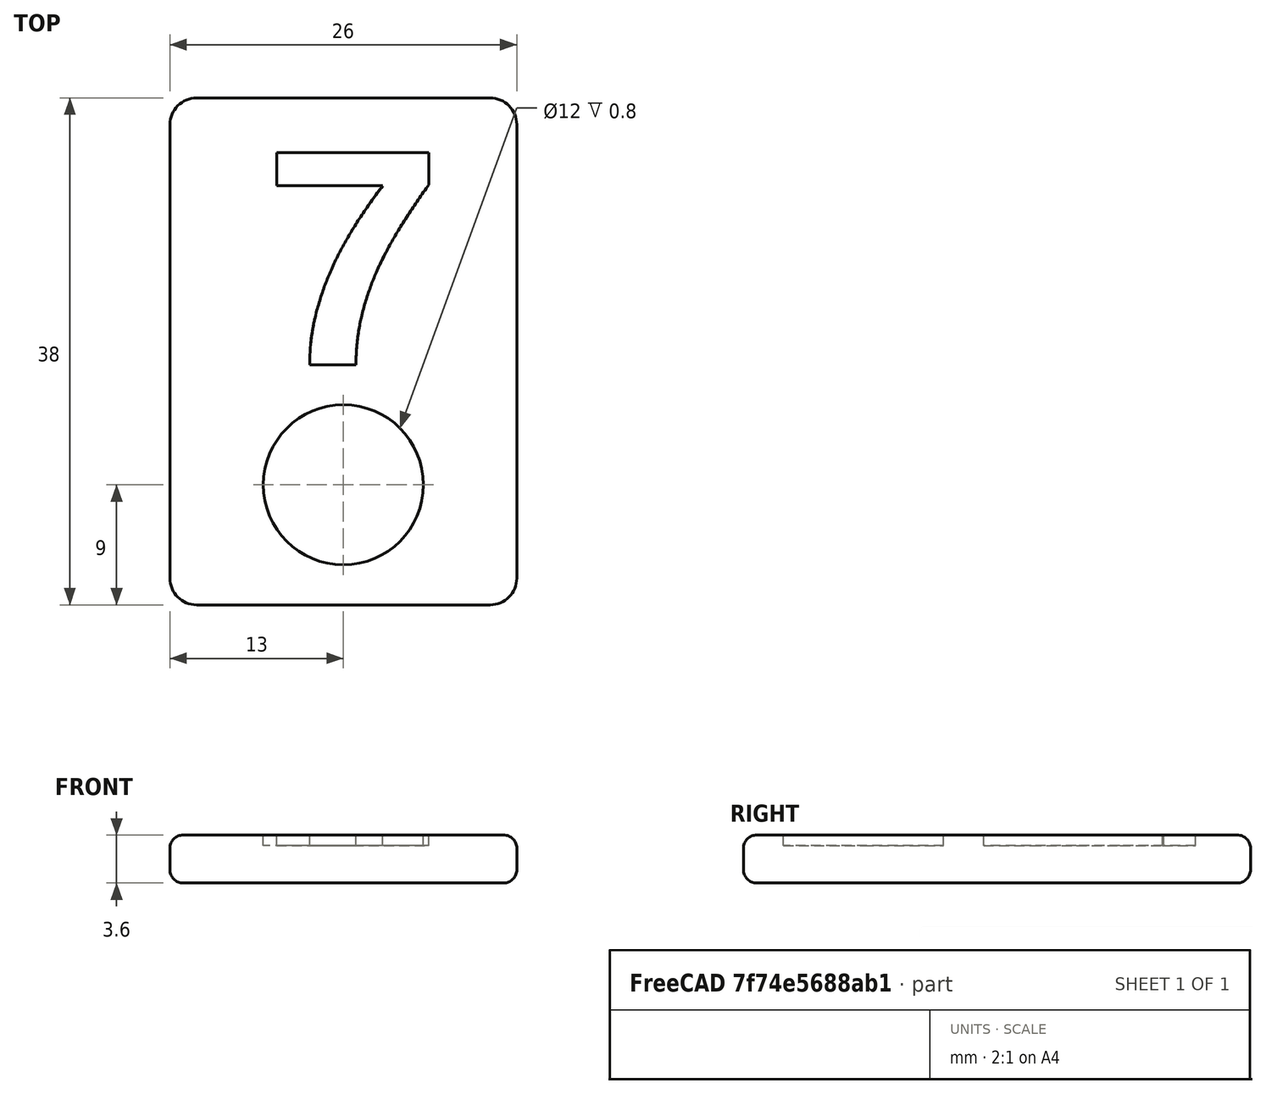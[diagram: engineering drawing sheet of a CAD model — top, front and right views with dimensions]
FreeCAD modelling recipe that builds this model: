
FCSTD DOCUMENT  (FreeCAD 0.14R3702 (Git))
Label: ficha7
License: CC-BY 3.0
LicenseURL: http://creativecommons.org/licenses/by/3.0/
objects: Part::Fillet×2, Part::Cut×2, Part::Box×1, Part::Part2DObjectPython×1, Part::Cylinder×1, Part::Extrusion×1
note: 8 computed .brp shape members not serialized (recipe doc carries the construction recipe); baked Part::Feature solids carry a one-line shape summary decoded from their .brp

FEATURE [Part::Box] Box  label="Cubo"
  Height = 3.6
  Length = 26
  Width = 38
FEATURE [Part::Fillet] Fillet
  Base = -> Box
  Edges = 4 edges r=2: [Edge1,Edge3,Edge5,Edge7]
FEATURE [Part::Part2DObjectPython] ShapeString  # Draft 2D object (typed FeaturePython)
  FontFile = <path>
  Placement = pos=(6.5,18,4) rot=(0,0,1;0rad)
  Size = 18
  String = 7
  Tracking = 0
FEATURE [Part::Cylinder] Cylinder  label="Cilindro"
  Angle = 360
  Height = 10
  Placement = pos=(13,9,2.8) rot=(0,0,1;0rad)
  Radius = 6
FEATURE [Part::Extrusion] Extrude001
  Base = -> ShapeString
  Dir = (0,0,2)
  Placement = pos=(0,0,-1.2) rot=(0,0,1;0rad)
  Solid = true
FEATURE [Part::Cut] Cut
  Base = -> Fillet
  Tool = -> Cylinder
FEATURE [Part::Cut] Cut001
  Base = -> Cut
  Tool = -> Extrude001
FEATURE [Part::Fillet] Fillet001
  Base = -> Cut001
  Edges = 16 edges r=1: [Edge1,Edge4,Edge20,Edge21,Edge22,Edge23,Edge24,Edge25,Edge26,Edge27,Edge29,Edge31,Edge32,Edge33,Edge34,Edge35]
note: 1 file-system path scrubbed to <path> (originals preserved in the JSON sidecar)
